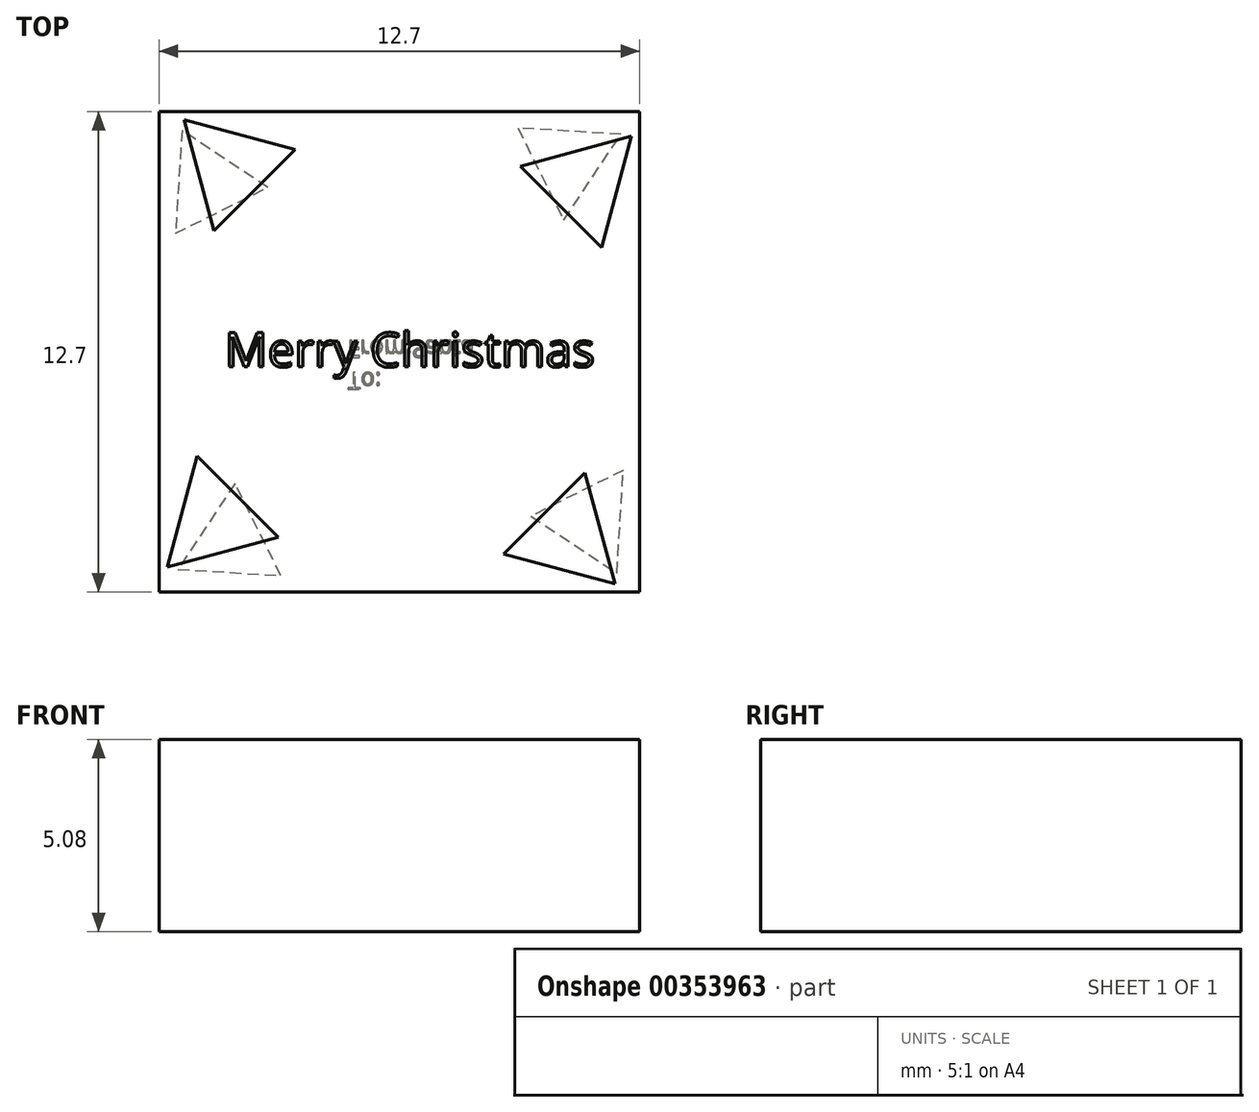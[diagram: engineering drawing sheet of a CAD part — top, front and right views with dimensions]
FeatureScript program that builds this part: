
annotation { "Feature Type Name" : "Feature", "Feature Type Description" : "" }
export const myFeature = defineFeature(function(context is Context, id is Id, definition is map)
    precondition{}
    {
        {
            var Q0;
            Q0=qCreatedBy(makeId("Top.planeOp"),FACE);
            var sketch = newSketch(context, id + "F0", { "sketchPlane" : qUnion([Q0])});
            skLineSegment(sketch, "E0.bottom", {"start": v(6.35, -6.35) * mm, "end": v(-6.35, -6.35) * mm});
            skLineSegment(sketch, "E0.top", {"start": v(6.35, 6.35) * mm, "end": v(-6.35, 6.35) * mm});
            skLineSegment(sketch, "E0.left", {"start": v(6.35, -6.35) * mm, "end": v(6.35, 6.35) * mm});
            skLineSegment(sketch, "E0.right", {"start": v(-6.35, -6.35) * mm, "end": v(-6.35, 6.35) * mm});
            skPoint(sketch, "E0.middle", {"position": v(0, 0) * mm});
            skSolve(sketch);
        }
        {
            var Q0;
            Q0 = qSketchRegion(id + "F0", true);
            extrude(context, id + "F1", {"entities" : qUnion([Q0]), "depth" : 5.08 * mm});
        }
        {
            var Q0;
            Q0=makeQuery(id+"F1.opExtrude","CAP_FACE",FACE,{"disambiguationData":[OSD([sQuery(id+"F0.wireOp",EDGE,"E0.bottom"),sQuery(id+"F0.wireOp",EDGE,"E0.top"),sQuery(id+"F0.wireOp",EDGE,"E0.left"),sQuery(id+"F0.wireOp",EDGE,"E0.right")])],"isStart":false});
            var sketch = newSketch(context, id + "F2", { "sketchPlane" : qUnion([Q0])});
            skCircle(sketch, "E1.cCircle", {"center": v(-4.45, 4.9) * mm, "radius": 0.88 * mm, "construction": true});
            skLineSegment(sketch, "E1.0", {"start": v(-2.76, 5.35) * mm, "end": v(-4.9, 3.2) * mm});
            skLineSegment(sketch, "E1.1", {"start": v(-4.9, 3.2) * mm, "end": v(-5.7, 6.14) * mm});
            skLineSegment(sketch, "E1.2", {"start": v(-5.7, 6.14) * mm, "end": v(-2.76, 5.35) * mm});
            skPoint(sketch, "E1.0.midPoint", {"position": v(-3.83, 4.27) * mm});
            skLineSegment(sketch, "E2.1.0", {"start": v(5.35, 2.76) * mm, "end": v(3.2, 4.9) * mm});
            skLineSegment(sketch, "E2.1.1", {"start": v(3.2, 4.9) * mm, "end": v(6.14, 5.7) * mm});
            skLineSegment(sketch, "E2.1.2", {"start": v(6.14, 5.7) * mm, "end": v(5.35, 2.76) * mm});
            skLineSegment(sketch, "E2.2.0", {"start": v(2.76, -5.35) * mm, "end": v(4.9, -3.2) * mm});
            skLineSegment(sketch, "E2.2.1", {"start": v(4.9, -3.2) * mm, "end": v(5.7, -6.14) * mm});
            skLineSegment(sketch, "E2.2.2", {"start": v(5.7, -6.14) * mm, "end": v(2.76, -5.35) * mm});
            skLineSegment(sketch, "E2.3.0", {"start": v(-5.35, -2.76) * mm, "end": v(-3.2, -4.9) * mm});
            skLineSegment(sketch, "E2.3.1", {"start": v(-3.2, -4.9) * mm, "end": v(-6.14, -5.7) * mm});
            skLineSegment(sketch, "E2.3.2", {"start": v(-6.14, -5.7) * mm, "end": v(-5.35, -2.76) * mm});
            skPoint(sketch, "E2.center", {"position": v(0, 0) * mm});
            skLineSegment(sketch, "E2.anchor1", {"start": v(0, 0) * mm, "end": v(-4.9, 3.2) * mm, "construction": true});
            skLineSegment(sketch, "E2.anchor2", {"start": v(0, 0) * mm, "end": v(-3.2, -4.9) * mm, "construction": true});
            skSolve(sketch);
        }
        {
            var Q0;
            Q0 = qSketchRegion(id + "F2", true);
            extrude(context, id + "F3", {"entities" : qUnion([Q0]), "operationType" : NewBodyOperationType.ADD, "depth" : 0 * mm});
        }
        {
            var Q0;
            Q0=makeQuery(id+"F1.opExtrude","CAP_FACE",FACE,{"disambiguationData":[OSD([sQuery(id+"F0.wireOp",EDGE,"E0.bottom"),sQuery(id+"F0.wireOp",EDGE,"E0.top"),sQuery(id+"F0.wireOp",EDGE,"E0.left"),sQuery(id+"F0.wireOp",EDGE,"E0.right")])],"isStart":true});
            var sketch = newSketch(context, id + "F4", { "sketchPlane" : qUnion([Q0])});
            skCircle(sketch, "E3.cCircle", {"center": v(-4.45, 5.05) * mm, "radius": 0.79 * mm, "construction": true});
            skLineSegment(sketch, "E3.0", {"start": v(-3.13, 5.92) * mm, "end": v(-4.35, 3.47) * mm});
            skLineSegment(sketch, "E3.1", {"start": v(-4.35, 3.47) * mm, "end": v(-5.86, 5.75) * mm});
            skLineSegment(sketch, "E3.2", {"start": v(-5.86, 5.75) * mm, "end": v(-3.13, 5.92) * mm});
            skPoint(sketch, "E3.0.midPoint", {"position": v(-3.74, 4.7) * mm});
            skLineSegment(sketch, "E4.1.0", {"start": v(3.47, 4.35) * mm, "end": v(5.75, 5.86) * mm});
            skLineSegment(sketch, "E4.1.1", {"start": v(5.75, 5.86) * mm, "end": v(5.92, 3.13) * mm});
            skLineSegment(sketch, "E4.1.2", {"start": v(5.92, 3.13) * mm, "end": v(3.47, 4.35) * mm});
            skLineSegment(sketch, "E4.2.0", {"start": v(4.35, -3.47) * mm, "end": v(5.86, -5.75) * mm});
            skLineSegment(sketch, "E4.2.1", {"start": v(5.86, -5.75) * mm, "end": v(3.13, -5.92) * mm});
            skLineSegment(sketch, "E4.2.2", {"start": v(3.13, -5.92) * mm, "end": v(4.35, -3.47) * mm});
            skLineSegment(sketch, "E4.3.0", {"start": v(-3.47, -4.35) * mm, "end": v(-5.75, -5.86) * mm});
            skLineSegment(sketch, "E4.3.1", {"start": v(-5.75, -5.86) * mm, "end": v(-5.92, -3.13) * mm});
            skLineSegment(sketch, "E4.3.2", {"start": v(-5.92, -3.13) * mm, "end": v(-3.47, -4.35) * mm});
            skPoint(sketch, "E4.center", {"position": v(0, 0) * mm});
            skLineSegment(sketch, "E4.anchor1", {"start": v(0, 0) * mm, "end": v(-4.35, 3.47) * mm, "construction": true});
            skLineSegment(sketch, "E4.anchor2", {"start": v(0, 0) * mm, "end": v(-3.47, -4.35) * mm, "construction": true});
            skSolve(sketch);
        }
        {
            var Q0;
            Q0 = qSketchRegion(id + "F4", true);
            extrude(context, id + "F5", {"entities" : qUnion([Q0]), "operationType" : NewBodyOperationType.ADD, "depth" : 0 * mm});
        }
        {
            var Q0;
            Q0=makeQuery(id+"F1.opExtrude","CAP_FACE",FACE,{"disambiguationData":[OSD([sQuery(id+"F0.wireOp",EDGE,"E0.bottom"),sQuery(id+"F0.wireOp",EDGE,"E0.top"),sQuery(id+"F0.wireOp",EDGE,"E0.left"),sQuery(id+"F0.wireOp",EDGE,"E0.right")])],"isStart":true});
            var sketch = newSketch(context, id + "F6", { "sketchPlane" : qUnion([Q0])});
            skText(sketch, "E5", { "text": "To:\nFrom:Santa", "fontName": "OpenSans-Regular.ttf"});
            const initialGuessF6  = {"E5": [-0.00137, 0.00055, 1, 0, 0.00045]};
            skSetInitialGuess(sketch, initialGuessF6);
            skSolve(sketch);
        }
        {
            var Q0;
            Q0 = qSketchRegion(id + "F6", true);
            extrude(context, id + "F7", {"entities" : qUnion([Q0]), "operationType" : NewBodyOperationType.ADD, "depth" : 0 * mm});
        }
        {
            var Q0;
            Q0=makeQuery(id+"F1.opExtrude","CAP_FACE",FACE,{"disambiguationData":[OSD([sQuery(id+"F0.wireOp",EDGE,"E0.bottom"),sQuery(id+"F0.wireOp",EDGE,"E0.top"),sQuery(id+"F0.wireOp",EDGE,"E0.left"),sQuery(id+"F0.wireOp",EDGE,"E0.right")])],"isStart":false});
            var sketch = newSketch(context, id + "F8", { "sketchPlane" : qUnion([Q0])});
            skText(sketch, "E6", { "text": "Merry Christmas", "fontName": "OpenSans-Regular.ttf"});
            const initialGuessF8  = {"E6": [-0.00462, -0.0004, 1, 0, 0.00091]};
            skSetInitialGuess(sketch, initialGuessF8);
            skSolve(sketch);
        }
        {
            var Q0;
            Q0 = qSketchRegion(id + "F8", true);
            extrude(context, id + "F9", {"entities" : qUnion([Q0]), "operationType" : NewBodyOperationType.ADD, "depth" : 0 * mm});
        }
    });
